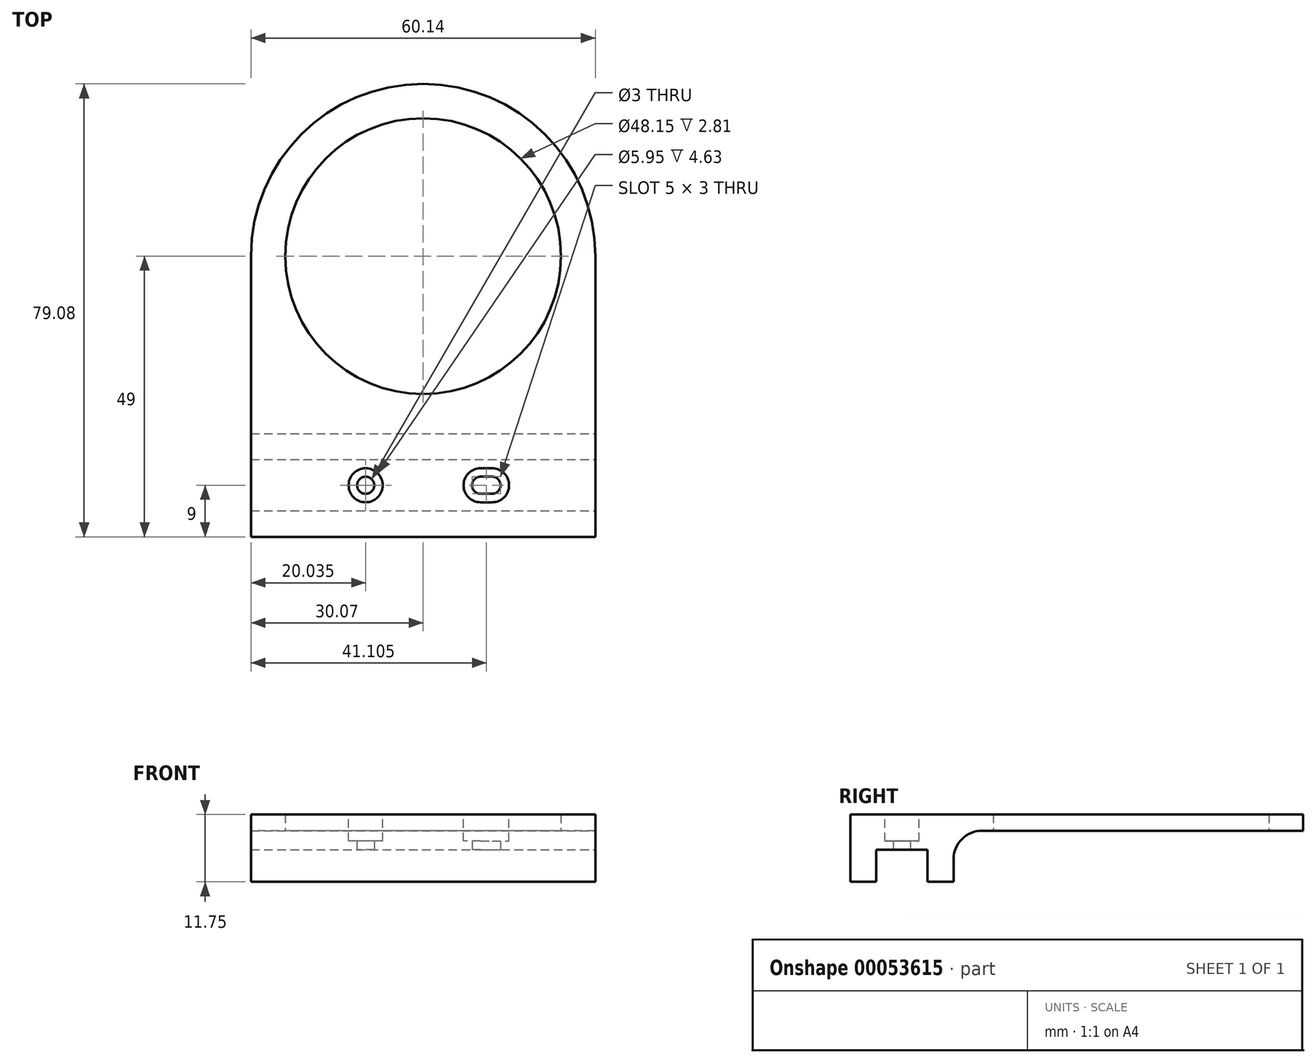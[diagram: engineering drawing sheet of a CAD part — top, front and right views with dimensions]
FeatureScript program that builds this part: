
annotation { "Feature Type Name" : "Feature", "Feature Type Description" : "" }
export const myFeature = defineFeature(function(context is Context, id is Id, definition is map)
    precondition{}
    {
        {
            var Q0;
            Q0=qCreatedBy(makeId("Top.planeOp"),FACE);
            var sketch = newSketch(context, id + "F0", { "sketchPlane" : qUnion([Q0])});
            skCircle(sketch, "E0", {"center": v(0, 0) * mm, "radius": 24.07 * mm});
            skCircle(sketch, "E1.0", {"center": v(0, 0) * mm, "radius": 30.07 * mm});
            skLineSegment(sketch, "E2", {"start": v(-44.24, -40) * mm, "end": v(60.93, -40) * mm, "construction": true});
            skCircle(sketch, "E3", {"center": v(-10.03, -40) * mm, "radius": 1.5 * mm});
            skCircle(sketch, "E4", {"center": v(10.04, -40) * mm, "radius": 1.5 * mm});
            skLineSegment(sketch, "E5", {"start": v(-30.07, 0) * mm, "end": v(-30.07, -54) * mm});
            skLineSegment(sketch, "E6", {"start": v(-30.07, -54) * mm, "end": v(30.08, -54) * mm});
            skLineSegment(sketch, "E7", {"start": v(30.08, -54) * mm, "end": v(30.07, 0) * mm});
            skLineSegment(sketch, "E8.bottom", {"start": v(-41.6, -35.52) * mm, "end": v(53.2, -35.52) * mm});
            skLineSegment(sketch, "E8.top", {"start": v(-41.6, -44.47) * mm, "end": v(53.2, -44.47) * mm});
            skLineSegment(sketch, "E8.left", {"start": v(-41.6, -35.53) * mm, "end": v(-41.6, -44.47) * mm});
            skLineSegment(sketch, "E8.right", {"start": v(53.2, -35.53) * mm, "end": v(53.2, -44.47) * mm});
            skLineSegment(sketch, "E9", {"start": v(-41.6, -40) * mm, "end": v(53.2, -40) * mm, "construction": true});
            skLineSegment(sketch, "E10.bottom", {"start": v(-44.24, -31) * mm, "end": v(39.26, -31) * mm});
            skLineSegment(sketch, "E10.top", {"start": v(-44.24, -49) * mm, "end": v(39.26, -49) * mm});
            skLineSegment(sketch, "E10.left", {"start": v(-44.24, -31) * mm, "end": v(-44.24, -49) * mm});
            skLineSegment(sketch, "E10.right", {"start": v(39.26, -31) * mm, "end": v(39.26, -49) * mm});
            skCircle(sketch, "E11", {"center": v(12.04, -40) * mm, "radius": 1.5 * mm});
            skLineSegment(sketch, "E12", {"start": v(10.04, -41.5) * mm, "end": v(12.04, -41.5) * mm});
            skLineSegment(sketch, "E13.MirrorCS", {"start": v(10.04, -38.5) * mm, "end": v(12.04, -38.5) * mm});
            skSolve(sketch);
        }
        {
            var Q0;
            Q0=makeQuery(id+"F0.imprint","IMPRINT",FACE,{"disambiguationData":[TD([[makeQuery(id+"F0.imprint","IMPRINT",EDGE,{"derivedFrom":sQuery(id+"F0.wireOp",EDGE,"E0")}),-1.0]])]});
            var Q1;
            {var subQ0=sQuery(id+"F0.wireOp",EDGE,"E5");var subQ1=sQuery(id+"F0.wireOp",EDGE,"E1.0");var subQ2=makeQuery(id+"F0.imprint","INTERSECT",VERTEX,{"derivedFrom":[subQ1,subQ0]});Q1=makeQuery(id+"F0.imprint","IMPRINT",FACE,{"disambiguationData":[TD([[makeQuery(id+"F0.imprint","IMPRINT",EDGE,{"disambiguationData":[TD([[subQ2,-1.0]])],"derivedFrom":subQ1}),-1.0]])]});}
            var Q2;
            {var subQ0=sQuery(id+"F0.wireOp",EDGE,"E10.bottom");var subQ1=sQuery(id+"F0.wireOp",EDGE,"E5");var subQ2=makeQuery(id+"F0.imprint","INTERSECT",VERTEX,{"derivedFrom":[subQ1,subQ0]});Q2=makeQuery(id+"F0.imprint","IMPRINT",FACE,{"disambiguationData":[TD([[makeQuery(id+"F0.imprint","IMPRINT",EDGE,{"disambiguationData":[TD([[subQ2,-1.0]])],"derivedFrom":subQ1}),1.0]])]});}
            var Q3;
            Q3=makeQuery(id+"F0.imprint","IMPRINT",FACE,{"disambiguationData":[TD([[makeQuery(id+"F0.imprint","IMPRINT",EDGE,{"derivedFrom":sQuery(id+"F0.wireOp",EDGE,"E3")}),-1.0]])]});
            var Q4;
            {var subQ0=sQuery(id+"F0.wireOp",EDGE,"E10.top");var subQ1=sQuery(id+"F0.wireOp",EDGE,"E5");var subQ2=makeQuery(id+"F0.imprint","INTERSECT",VERTEX,{"derivedFrom":[subQ1,subQ0]});Q4=makeQuery(id+"F0.imprint","IMPRINT",FACE,{"disambiguationData":[TD([[makeQuery(id+"F0.imprint","IMPRINT",EDGE,{"disambiguationData":[TD([[subQ2,1.0]])],"derivedFrom":subQ1}),1.0]])]});}
            extrude(context, id + "F1", {"entities" : qUnion([Q0, Q1, Q2, Q3, Q4]), "depth" : 11.75 * mm});
        }
        {
            var Q0;
            Q0=makeQuery(id+"F0.imprint","IMPRINT",FACE,{"disambiguationData":[TD([[makeQuery(id+"F0.imprint","IMPRINT",EDGE,{"derivedFrom":sQuery(id+"F0.wireOp",EDGE,"E3")}),-1.0]])]});
            extrude(context, id + "F2", {"entities" : qUnion([Q0]), "operationType" : NewBodyOperationType.REMOVE, "depth" : 5.62 * mm});
        }
        {
            var Q0;
            Q0=makeQuery(id+"F1.opExtrude","CAP_FACE",FACE,{"disambiguationData":[OSD([sQuery(id+"F0.wireOp",EDGE,"E0"),sQuery(id+"F0.wireOp",EDGE,"E1.0"),sQuery(id+"F0.wireOp",EDGE,"E3"),sQuery(id+"F0.wireOp",EDGE,"E4"),sQuery(id+"F0.wireOp",EDGE,"E5"),sQuery(id+"F0.wireOp",EDGE,"E6"),sQuery(id+"F0.wireOp",EDGE,"E7")])],"isStart":false});
            var sketch = newSketch(context, id + "F3", { "sketchPlane" : qUnion([Q0])});
            skCircle(sketch, "E14", {"center": v(-10.03, -40) * mm, "radius": 2.98 * mm});
            skArc(sketch, "E15.0", {"start": v(10.04, -38.5) * mm, "mid": v(8.54, -40) * mm, "end": v(10.04, -41.5) * mm});
            skLineSegment(sketch, "E15.1", {"start": v(10.04, -41.5) * mm, "end": v(12.04, -41.5) * mm});
            skLineSegment(sketch, "E15.2", {"start": v(10.04, -38.5) * mm, "end": v(12.04, -38.5) * mm});
            skArc(sketch, "E15.3", {"start": v(12.04, -41.5) * mm, "mid": v(13.54, -40) * mm, "end": v(12.04, -38.5) * mm});
            skArc(sketch, "E16.0", {"start": v(10.04, -37.03) * mm, "mid": v(7.06, -40) * mm, "end": v(10.04, -42.98) * mm});
            skLineSegment(sketch, "E16.1", {"start": v(10.04, -37.03) * mm, "end": v(12.04, -37.03) * mm});
            skArc(sketch, "E16.2", {"start": v(12.04, -42.98) * mm, "mid": v(15.01, -40) * mm, "end": v(12.04, -37.03) * mm});
            skLineSegment(sketch, "E16.3", {"start": v(10.04, -42.98) * mm, "end": v(12.04, -42.98) * mm});
            skSolve(sketch);
        }
        {
            var Q0;
            Q0 = qSketchRegion(id + "F3", true);
            extrude(context, id + "F4", {"entities" : qUnion([Q0]), "operationType" : NewBodyOperationType.REMOVE, "oppositeDirection" : true, "depth" : ((11.74 - 5.61) - 1.5) * mm});
        }
        {
            var Q0;
            Q0=makeQuery(id+"F0.imprint","IMPRINT",FACE,{"disambiguationData":[TD([[makeQuery(id+"F0.imprint","IMPRINT",EDGE,{"derivedFrom":sQuery(id+"F0.wireOp",EDGE,"E0")}),-1.0]])]});
            var Q1;
            {var subQ0=sQuery(id+"F0.wireOp",EDGE,"E5");var subQ1=sQuery(id+"F0.wireOp",EDGE,"E1.0");var subQ2=makeQuery(id+"F0.imprint","INTERSECT",VERTEX,{"derivedFrom":[subQ1,subQ0]});Q1=makeQuery(id+"F0.imprint","IMPRINT",FACE,{"disambiguationData":[TD([[makeQuery(id+"F0.imprint","IMPRINT",EDGE,{"disambiguationData":[TD([[subQ2,-1.0]])],"derivedFrom":subQ1}),-1.0]])]});}
            extrude(context, id + "F5", {"entities" : qUnion([Q0, Q1]), "operationType" : NewBodyOperationType.REMOVE, "depth" : 8.94 * mm});
        }
        {
            var Q0;
            Q0=makeQuery(id+"F5.boolean.opBoolean","COPY",EDGE,{"derivedFrom":makeQuery(id+"F5.opExtrude","CAP_EDGE",EDGE,{"disambiguationData":[OSD([sQuery(id+"F0.wireOp",EDGE,"E10.bottom")])],"isStart":false})});
            fillet(context, id + "F6", {"entities" : qUnion([Q0]), "radius" : 5 * mm, "tangentPropagation" : true, "allowEdgeOverflow" : false});
        }
    });
